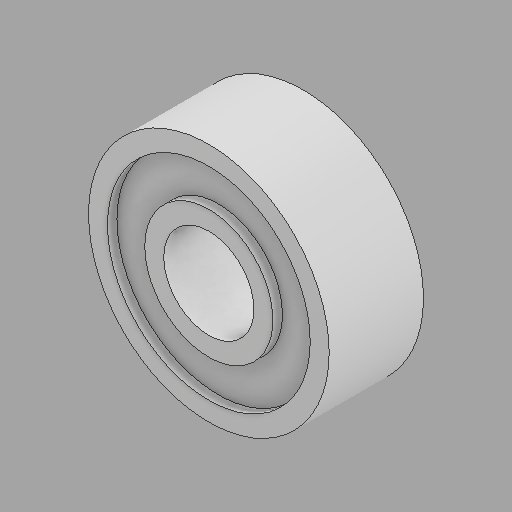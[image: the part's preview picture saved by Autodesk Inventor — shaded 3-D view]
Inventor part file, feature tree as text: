
AUTODESK INVENTOR PART (.ipt)
format: ipt  version: 2024.2 (Build 282272000, 272)  size: 135,680 bytes
history: native  units: in
note: dims shown in document units (in); Inventor stores cm internally (conversion verified against a paired STEP export)
features: revolve x1
ambient origin geometry x8: Origin, YZ Plane, XZ Plane, XY Plane, X Axis, Y Axis, Z Axis, Center Point
bodies: Solid1 (feature_tree)
feature tree (1):
  revolve  "Revolve1"  [1 undecoded]
note: 1 required parameter value undecoded (feature->parameter linkage not recoverable at this tier; creation-order binding heuristic only, values carry confidence <= 0.55)
